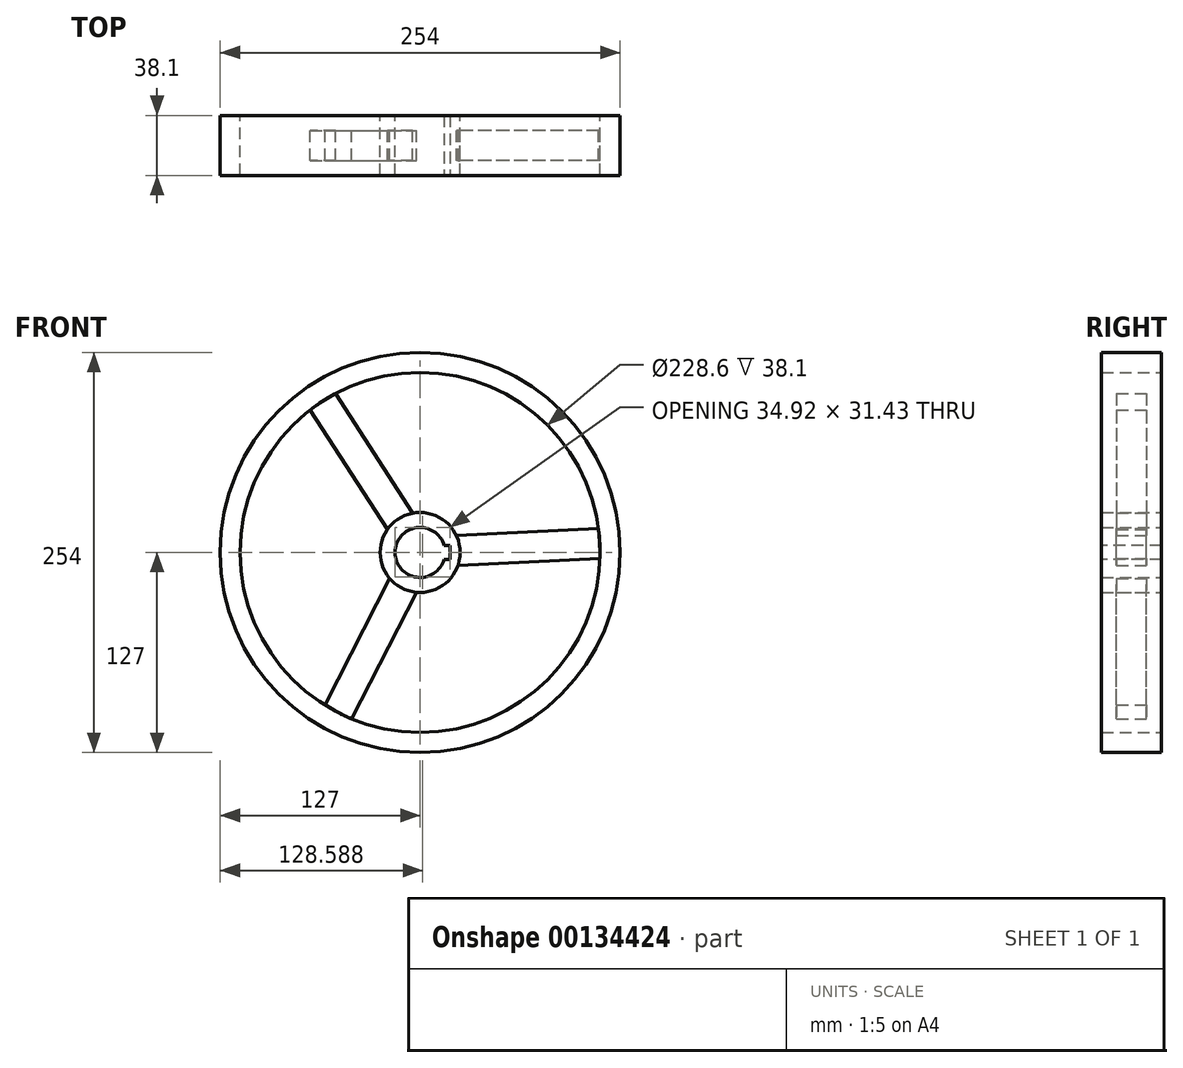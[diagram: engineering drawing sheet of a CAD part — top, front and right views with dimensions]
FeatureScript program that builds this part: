
annotation { "Feature Type Name" : "Feature", "Feature Type Description" : "" }
export const myFeature = defineFeature(function(context is Context, id is Id, definition is map)
    precondition{}
    {
        {
            var Q0;
            Q0=qCreatedBy(makeId("Front.planeOp"),FACE);
            var sketch = newSketch(context, id + "F0", { "sketchPlane" : qUnion([Q0])});
            skCircle(sketch, "E0", {"center": v(0, 0) * mm, "radius": 15.88 * mm});
            skCircle(sketch, "E1", {"center": v(0, 0) * mm, "radius": 25.4 * mm});
            skCircle(sketch, "E2", {"center": v(0, 0) * mm, "radius": 114.3 * mm});
            skCircle(sketch, "E3", {"center": v(0, 0) * mm, "radius": 127 * mm});
            skSolve(sketch);
        }
        {
            var Q0;
            Q0=makeQuery(id+"F0.imprint","IMPRINT",FACE,{"disambiguationData":[TD([[makeQuery(id+"F0.imprint","IMPRINT",EDGE,{"derivedFrom":sQuery(id+"F0.wireOp",EDGE,"E2")}),-1.0]])]});
            var Q1;
            Q1=makeQuery(id+"F0.imprint","IMPRINT",FACE,{"disambiguationData":[TD([[makeQuery(id+"F0.imprint","IMPRINT",EDGE,{"derivedFrom":sQuery(id+"F0.wireOp",EDGE,"E0")}),-1.0]])]});
            extrude(context, id + "F1", {"entities" : qUnion([Q0, Q1]), "endBound" : BoundingType.SYMMETRIC, "depth" : 38.1 * mm});
        }
        {
            var Q0;
            Q0=qCreatedBy(makeId("Front.planeOp"),FACE);
            var sketch = newSketch(context, id + "F2", { "sketchPlane" : qUnion([Q0])});
            skCircle(sketch, "E4.0", {"center": v(0, 0) * mm, "radius": 25.4 * mm});
            skCircle(sketch, "E5.0", {"center": v(0, 0) * mm, "radius": 114.3 * mm});
            skLineSegment(sketch, "E6", {"start": v(-69.76, 90.54) * mm, "end": v(-20.74, 14.66) * mm});
            skLineSegment(sketch, "E7", {"start": v(-53.75, 100.87) * mm, "end": v(-4.72, 24.96) * mm});
            skLineSegment(sketch, "E8", {"start": v(0, 0) * mm, "end": v(-62.02, 96.01) * mm, "construction": true});
            skSolve(sketch);
        }
        {
            var Q0;
            {var subQ0=sQuery(id+"F2.wireOp",EDGE,"E6");Q0=makeQuery(id+"F2.imprint","IMPRINT",FACE,{"disambiguationData":[TD([[makeQuery(id+"F2.imprint","IMPRINT",EDGE,{"derivedFrom":subQ0}),1.0]])]});}
            extrude(context, id + "F3", {"entities" : qUnion([Q0]), "endBound" : BoundingType.SYMMETRIC, "depth" : 19.05 * mm});
        }
        {
            var Q0;
            Q0=makeQuery(id+"F3.opExtrude","SWEPT_BODY",BODY,{"disambiguationData":[OSD([sQuery(id+"F2.wireOp",EDGE,"E4.0"),sQuery(id+"F2.wireOp",EDGE,"E5.0"),sQuery(id+"F2.wireOp",EDGE,"E6"),sQuery(id+"F2.wireOp",EDGE,"E7")])]});
            var Q1;
            Q1=sQuery(id+"F2.wireOp",EDGE,"E4.0");
            circularPattern(context, id + "F4", {"entities" : qUnion([Q0]), "axis" : qUnion([Q1]), "angle" : 120 * degree, "instanceCount" : 3});
        }
        {
            var Q0;
            Q0=makeQuery(id+"F1.opExtrude","CAP_FACE",FACE,{"disambiguationData":[OSD([sQuery(id+"F0.wireOp",EDGE,"E0"),sQuery(id+"F0.wireOp",EDGE,"E1")])],"isStart":false});
            var sketch = newSketch(context, id + "F5", { "sketchPlane" : qUnion([Q0])});
            skCircle(sketch, "E9.0", {"center": v(0, 0) * mm, "radius": 15.88 * mm});
            skLineSegment(sketch, "E10.bottom", {"start": v(15.24, 4.45) * mm, "end": v(19.05, 4.45) * mm});
            skLineSegment(sketch, "E10.top", {"start": v(15.24, -4.44) * mm, "end": v(19.05, -4.44) * mm});
            skLineSegment(sketch, "E10.left", {"start": v(15.24, 4.44) * mm, "end": v(15.24, -4.44) * mm});
            skLineSegment(sketch, "E10.right", {"start": v(19.05, 4.44) * mm, "end": v(19.05, -4.44) * mm});
            skSolve(sketch);
        }
        {
            var Q0;
            {var subQ0=sQuery(id+"F5.wireOp",EDGE,"E10.left");Q0=makeQuery(id+"F5.imprint","IMPRINT",FACE,{"disambiguationData":[TD([[makeQuery(id+"F5.imprint","IMPRINT",EDGE,{"derivedFrom":subQ0}),1.0]])]});}
            var Q1;
            {var subQ1=sQuery(id+"F5.wireOp",EDGE,"E10.bottom");Q1=makeQuery(id+"F5.imprint","IMPRINT",FACE,{"disambiguationData":[TD([[makeQuery(id+"F5.imprint","IMPRINT",EDGE,{"derivedFrom":subQ1}),-1.0]])]});}
            extrude(context, id + "F6", {"entities" : qUnion([Q0, Q1]), "operationType" : NewBodyOperationType.REMOVE, "endBound" : BoundingType.THROUGH_ALL, "oppositeDirection" : true, "depth" : 25.4 * mm});
        }
    });
